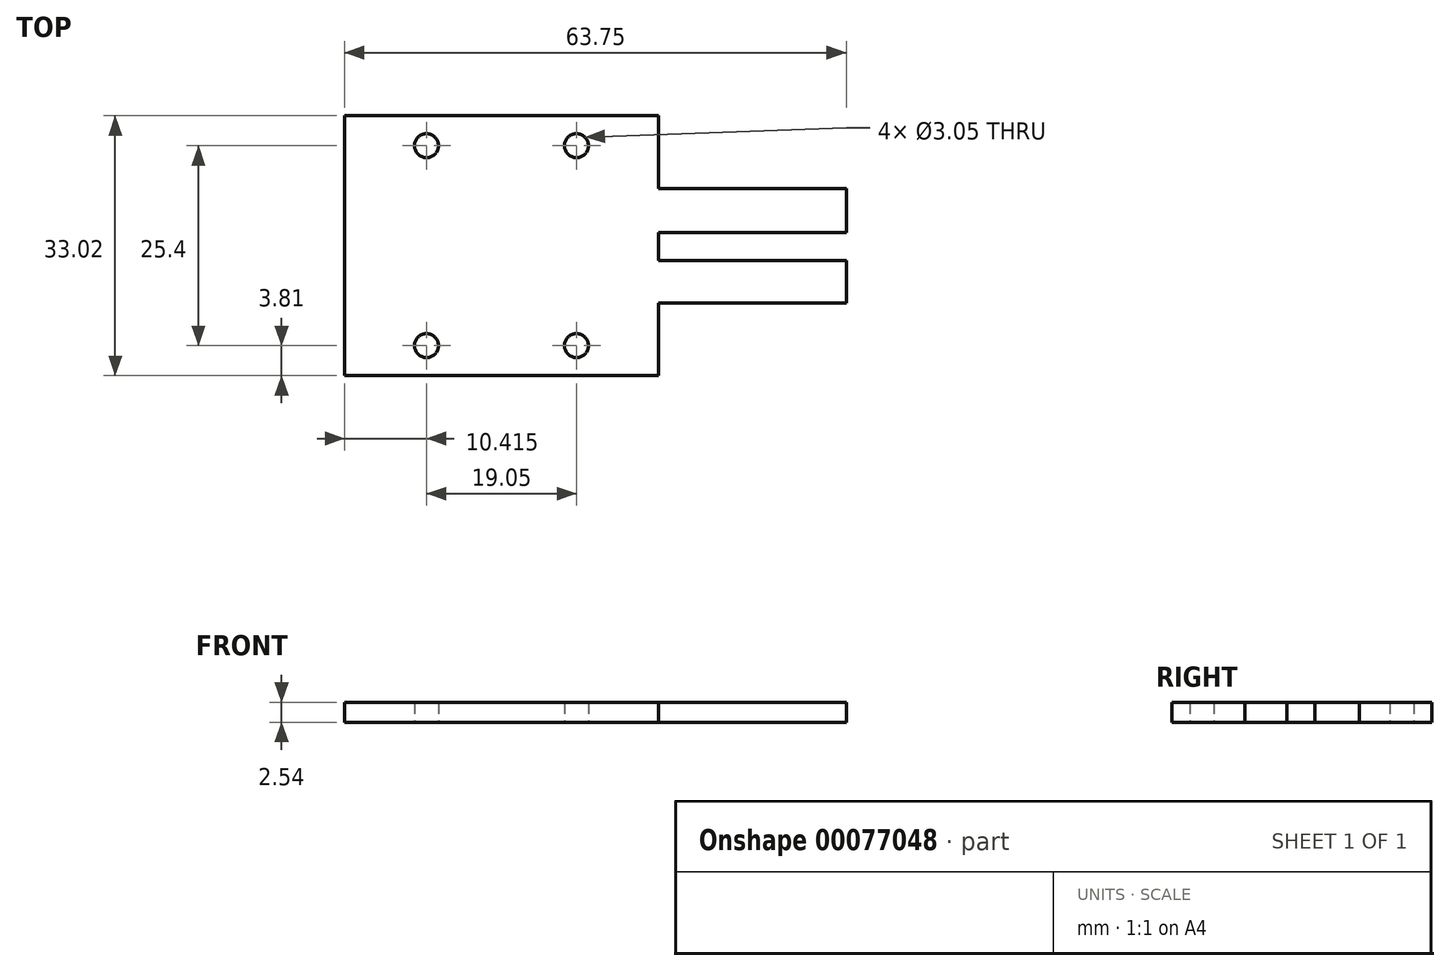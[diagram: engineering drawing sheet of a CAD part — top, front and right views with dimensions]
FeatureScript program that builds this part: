
annotation { "Feature Type Name" : "Feature", "Feature Type Description" : "" }
export const myFeature = defineFeature(function(context is Context, id is Id, definition is map)
    precondition{}
    {
        {
            var Q0;
            Q0=qCreatedBy(makeId("Top.planeOp"),FACE);
            var sketch = newSketch(context, id + "F0", { "sketchPlane" : qUnion([Q0])});
            skLineSegment(sketch, "E0.bottom", {"start": v(-19.94, 16.51) * mm, "end": v(19.94, 16.51) * mm});
            skLineSegment(sketch, "E0.top", {"start": v(-19.94, -16.51) * mm, "end": v(19.94, -16.51) * mm});
            skLineSegment(sketch, "E0.left", {"start": v(-19.94, 16.51) * mm, "end": v(-19.94, -16.51) * mm});
            skPoint(sketch, "E0.middle", {"position": v(0, 0) * mm});
            skPoint(sketch, "E1.middle", {"position": v(0, 16.51) * mm});
            skLineSegment(sketch, "E2", {"start": v(0, 34) * mm, "end": v(0, -24.9) * mm, "construction": true});
            skPoint(sketch, "E3.middle", {"position": v(-19.94, 0) * mm});
            skCircle(sketch, "E4", {"center": v(-9.52, 12.7) * mm, "radius": 1.52 * mm});
            skCircle(sketch, "E5.MirrorC", {"center": v(9.52, 12.7) * mm, "radius": 1.52 * mm});
            skCircle(sketch, "E6.MirrorC", {"center": v(-9.53, -12.7) * mm, "radius": 1.52 * mm});
            skCircle(sketch, "E7.MirrorC", {"center": v(9.52, -12.7) * mm, "radius": 1.52 * mm});
            skPoint(sketch, "E8.middle", {"position": v(0, -14.76) * mm});
            skPoint(sketch, "E9.middle", {"position": v(19.94, 0) * mm});
            skLineSegment(sketch, "E10", {"start": v(19.94, 7.26) * mm, "end": v(43.81, 7.26) * mm});
            skLineSegment(sketch, "E11", {"start": v(43.81, 1.65) * mm, "end": v(19.94, 1.65) * mm});
            skLineSegment(sketch, "E12", {"start": v(19.94, -1.9) * mm, "end": v(43.81, -1.9) * mm});
            skLineSegment(sketch, "E13", {"start": v(43.81, -7.26) * mm, "end": v(19.94, -7.26) * mm});
            skLineSegment(sketch, "E14", {"start": v(19.94, 16.51) * mm, "end": v(19.94, 7.26) * mm});
            skLineSegment(sketch, "E15", {"start": v(19.94, -7.26) * mm, "end": v(19.94, -16.51) * mm});
            skLineSegment(sketch, "E16", {"start": v(19.94, 1.65) * mm, "end": v(19.94, -1.9) * mm});
            skLineSegment(sketch, "E17", {"start": v(43.81, 7.26) * mm, "end": v(43.81, 1.65) * mm});
            skLineSegment(sketch, "E18", {"start": v(43.81, -1.9) * mm, "end": v(43.81, -7.26) * mm});
            skSolve(sketch);
        }
        {
            var Q0;
            Q0=makeQuery(id+"F0.imprint","IMPRINT",FACE,{"disambiguationData":[TD([[makeQuery(id+"F0.imprint","IMPRINT",EDGE,{"derivedFrom":sQuery(id+"F0.wireOp",EDGE,"E0.bottom")}),-1.0]])]});
            extrude(context, id + "F1", {"entities" : qUnion([Q0]), "depth" : 2.54 * mm});
        }
    });
